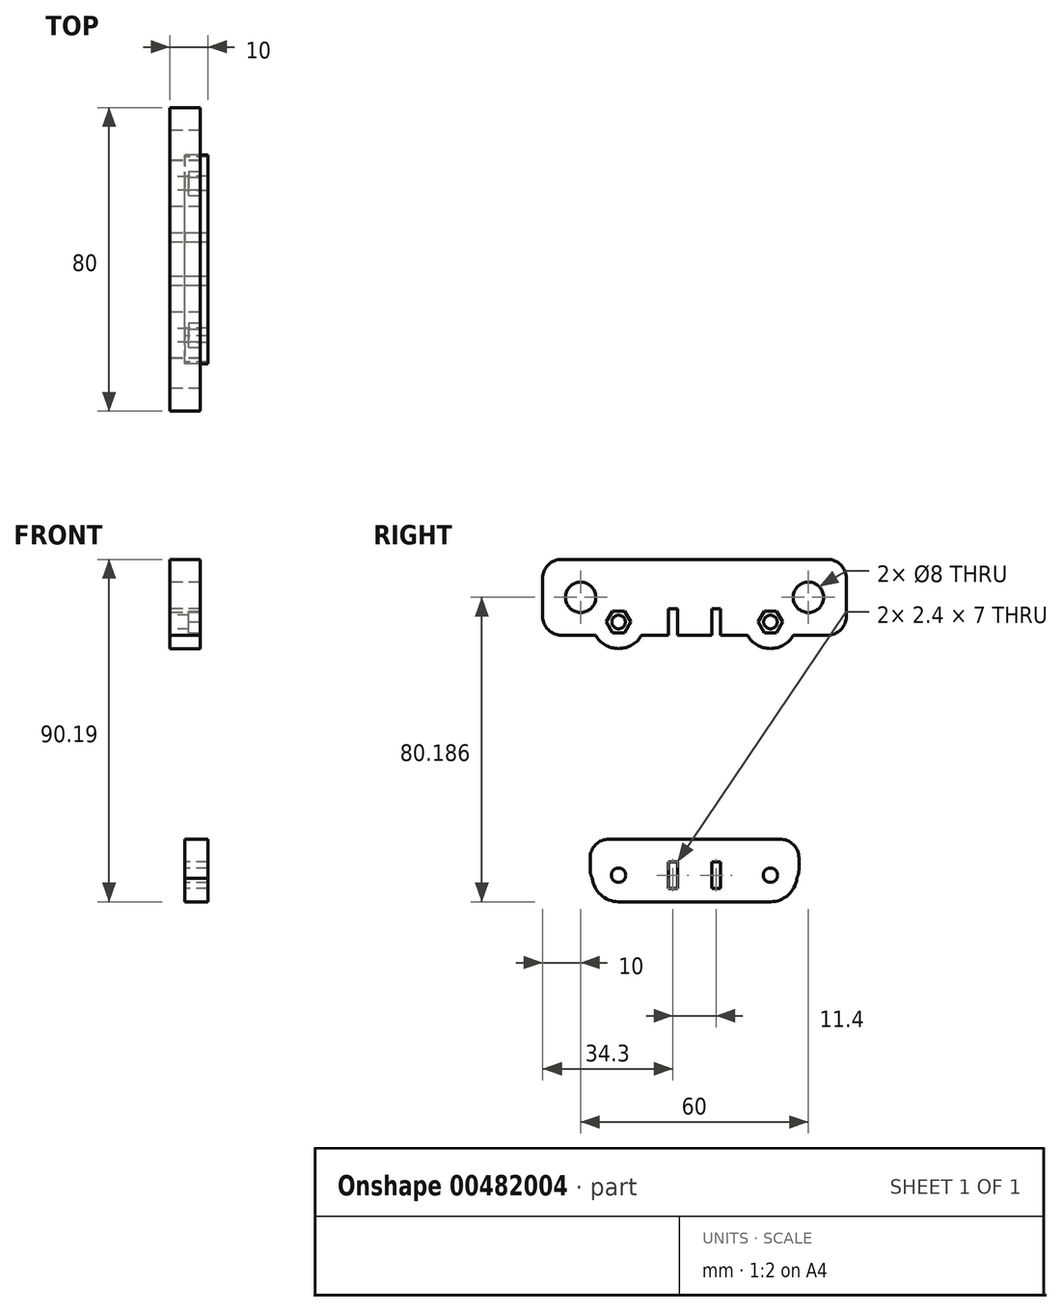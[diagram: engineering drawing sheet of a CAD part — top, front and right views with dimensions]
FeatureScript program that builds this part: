
annotation { "Feature Type Name" : "Feature", "Feature Type Description" : "" }
export const myFeature = defineFeature(function(context is Context, id is Id, definition is map)
    precondition{}
    {
        {
            var Q0;
            Q0=qCreatedBy(makeId("Right.planeOp"),FACE);
            var sketch = newSketch(context, id + "F0", { "sketchPlane" : qUnion([Q0])});
            skLineSegment(sketch, "E0", {"start": v(0, 142.5) * mm, "end": v(0, -139.74) * mm, "construction": true});
            skLineSegment(sketch, "E1.bottom", {"start": v(-35, 25) * mm, "end": v(35, 25) * mm});
            skLineSegment(sketch, "E1.top", {"start": v(-40, -25) * mm, "end": v(40, -25) * mm});
            skLineSegment(sketch, "E1.left", {"start": v(-40, 20) * mm, "end": v(-40, -25) * mm});
            skLineSegment(sketch, "E1.right", {"start": v(40, 20) * mm, "end": v(40, -25) * mm});
            skPoint(sketch, "E1.middle", {"position": v(0, 0) * mm});
            skCircle(sketch, "E2", {"center": v(-30, 13) * mm, "radius": 4 * mm});
            skCircle(sketch, "E3", {"center": v(30, 13) * mm, "radius": 4 * mm});
            skCircle(sketch, "E4", {"center": v(-30, -13) * mm, "radius": 5 * mm});
            skCircle(sketch, "E5", {"center": v(30, -13) * mm, "radius": 5 * mm});
            skPoint(sketch, "E6.visualSharp", {"position": v(-40, 25) * mm});
            skArc(sketch, "E6.filletArc", {"start": v(-35, 25) * mm, "mid": v(-38.54, 23.54) * mm, "end": v(-40, 20) * mm});
            skPoint(sketch, "E7.visualSharp", {"position": v(40, 25) * mm});
            skArc(sketch, "E7.filletArc", {"start": v(40, 20) * mm, "mid": v(38.54, 23.54) * mm, "end": v(35, 25) * mm});
            skLineSegment(sketch, "E8.bottom", {"start": v(-11, 25) * mm, "end": v(11, 25) * mm});
            skLineSegment(sketch, "E8.top", {"start": v(-9, 8) * mm, "end": v(9, 8) * mm});
            skLineSegment(sketch, "E8.left", {"start": v(-11, 25) * mm, "end": v(-11, 10) * mm});
            skLineSegment(sketch, "E8.right", {"start": v(11, 25) * mm, "end": v(11, 10) * mm});
            skPoint(sketch, "E8.middle", {"position": v(0, 16.5) * mm});
            skPoint(sketch, "E9.visualSharp", {"position": v(11, 8) * mm});
            skArc(sketch, "E9.filletArc", {"start": v(9, 8) * mm, "mid": v(10.41, 8.59) * mm, "end": v(11, 10) * mm});
            skPoint(sketch, "E10.visualSharp", {"position": v(-11, 8) * mm});
            skArc(sketch, "E10.filletArc", {"start": v(-11, 10) * mm, "mid": v(-10.41, 8.59) * mm, "end": v(-9, 8) * mm});
            skSolve(sketch);
        }
        {
            var Q0;
            Q0=makeQuery(id+"F0.imprint","IMPRINT",FACE,{"disambiguationData":[TD([[makeQuery(id+"F0.imprint","IMPRINT",EDGE,{"derivedFrom":sQuery(id+"F0.wireOp",EDGE,"E1.bottom")}),-1.0]])]});
            extrude(context, id + "F1", {"entities" : qUnion([Q0]), "endBound" : BoundingType.SYMMETRIC, "depth" : 8 * mm});
        }
        {
            var Q0;
            {var subQ0=sQuery(id+"F0.wireOp",EDGE,"E1.bottom");Q0=makeQuery(id+"F1.opExtrude","SWEPT_FACE",FACE,{"disambiguationData":[OSD([subQ0]),TDD([makeQuery(id+"F0.imprint","IMPRINT",EDGE,{"disambiguationData":[TD([[makeQuery(id+"F0.imprint","INTERSECT",VERTEX,{"derivedFrom":[subQ0,sQuery(id+"F0.wireOp",EDGE,"E7.filletArc")]}),1.0]])],"derivedFrom":subQ0})])]});}
            var sketch = newSketch(context, id + "F2", { "sketchPlane" : qUnion([Q0])});
            skCircle(sketch, "E11", {"center": v(0, 30) * mm, "radius": 1.4 * mm});
            skCircle(sketch, "E12", {"center": v(0, 24) * mm, "radius": 1.4 * mm});
            skCircle(sketch, "E13", {"center": v(0, -24) * mm, "radius": 1.4 * mm});
            skCircle(sketch, "E14", {"center": v(0, -30) * mm, "radius": 1.4 * mm});
            skLineSegment(sketch, "E15", {"start": v(-76.86, 0) * mm, "end": v(82.98, 0) * mm, "construction": true});
            skSolve(sketch);
        }
        {
            var Q0;
            Q0=qSketchRegion(id+"F2",true);
            extrude(context, id + "F3", {"entities" : qUnion([Q0]), "operationType" : NewBodyOperationType.REMOVE, "oppositeDirection" : true, "depth" : 13 * mm});
        }
        {
            var Q0;
            Q0=qCreatedBy(makeId("Right.planeOp"),FACE);
            var sketch = newSketch(context, id + "F4", { "sketchPlane" : qUnion([Q0])});
            skLineSegment(sketch, "E16", {"start": v(0, 90) * mm, "end": v(0, 27.03) * mm, "construction": true});
            skCircle(sketch, "E17", {"center": v(-30, 70.19) * mm, "radius": 4 * mm});
            skCircle(sketch, "E18", {"center": v(30, 70.19) * mm, "radius": 4 * mm});
            skLineSegment(sketch, "E19.bottom", {"start": v(-35, 80.19) * mm, "end": v(35, 80.19) * mm});
            skLineSegment(sketch, "E19.top", {"start": v(-35, 60.19) * mm, "end": v(-26.06, 60.19) * mm});
            skLineSegment(sketch, "E19.left", {"start": v(-40, 75.19) * mm, "end": v(-40, 65.19) * mm});
            skLineSegment(sketch, "E19.right", {"start": v(40, 75.19) * mm, "end": v(40, 65.19) * mm});
            skPoint(sketch, "E19.middle", {"position": v(0, 70.19) * mm});
            skPoint(sketch, "E20.visualSharp", {"position": v(-40, 80.19) * mm});
            skArc(sketch, "E20.filletArc", {"start": v(-35, 80.19) * mm, "mid": v(-38.54, 78.72) * mm, "end": v(-40, 75.19) * mm});
            skPoint(sketch, "E21.visualSharp", {"position": v(-40, 60.19) * mm});
            skArc(sketch, "E21.filletArc", {"start": v(-40, 65.19) * mm, "mid": v(-38.54, 61.65) * mm, "end": v(-35, 60.19) * mm});
            skPoint(sketch, "E22.visualSharp", {"position": v(40, 80.19) * mm});
            skArc(sketch, "E22.filletArc", {"start": v(40, 75.19) * mm, "mid": v(38.54, 78.72) * mm, "end": v(35, 80.19) * mm});
            skPoint(sketch, "E23.visualSharp", {"position": v(40, 60.19) * mm});
            skArc(sketch, "E23.filletArc", {"start": v(35, 60.19) * mm, "mid": v(38.54, 61.65) * mm, "end": v(40, 65.19) * mm});
            skLineSegment(sketch, "E24.bottom", {"start": v(-11, 80.19) * mm, "end": v(11, 80.19) * mm});
            skPoint(sketch, "E24.middle", {"position": v(0, 76.69) * mm});
            skLineSegment(sketch, "E25", {"start": v(-87.97, 70.19) * mm, "end": v(-87.97, 70.19) * mm});
            skPoint(sketch, "E25.endSnap0", {"position": v(40, 70.19) * mm});
            skLineSegment(sketch, "E26.bottom", {"start": v(-6.9, 67.19) * mm, "end": v(-4.5, 67.19) * mm});
            skLineSegment(sketch, "E26.top", {"start": v(-6.9, 60.19) * mm, "end": v(-4.5, 60.19) * mm});
            skLineSegment(sketch, "E26.left", {"start": v(-6.9, 67.19) * mm, "end": v(-6.9, 60.19) * mm});
            skLineSegment(sketch, "E26.right", {"start": v(-4.5, 67.19) * mm, "end": v(-4.5, 60.19) * mm});
            skLineSegment(sketch, "E27.bottom", {"start": v(4.5, 67.19) * mm, "end": v(6.9, 67.19) * mm});
            skLineSegment(sketch, "E27.top", {"start": v(4.5, 60.19) * mm, "end": v(6.9, 60.19) * mm});
            skLineSegment(sketch, "E27.left", {"start": v(4.5, 67.19) * mm, "end": v(4.5, 60.19) * mm});
            skLineSegment(sketch, "E27.right", {"start": v(6.9, 67.19) * mm, "end": v(6.9, 60.19) * mm});
            skCircle(sketch, "E28", {"center": v(-20, 63.69) * mm, "radius": 1.8 * mm});
            skCircle(sketch, "E29", {"center": v(20, 63.69) * mm, "radius": 1.8 * mm});
            skArc(sketch, "E30", {"start": v(-26.06, 60.19) * mm, "mid": v(-20, 56.69) * mm, "end": v(-13.94, 60.19) * mm});
            skArc(sketch, "E31.MirrorC", {"start": v(26.06, 60.19) * mm, "mid": v(20, 56.69) * mm, "end": v(13.94, 60.19) * mm});
            skLineSegment(sketch, "E32.trimOffspring", {"start": v(-13.94, 60.19) * mm, "end": v(13.94, 60.19) * mm});
            skLineSegment(sketch, "E33.trimOffspring", {"start": v(26.06, 60.19) * mm, "end": v(35, 60.19) * mm});
            skSolve(sketch);
        }
        {
            var Q0;
            Q0=makeQuery(id+"F4.imprint","IMPRINT",FACE,{"disambiguationData":[TD([[makeQuery(id+"F4.imprint","IMPRINT",EDGE,{"derivedFrom":sQuery(id+"F4.wireOp",EDGE,"E17")}),-1.0]])]});
            extrude(context, id + "F5", {"entities" : qUnion([Q0]), "endBound" : BoundingType.SYMMETRIC, "depth" : 8 * mm});
        }
        {
            var Q0;
            Q0=makeQuery(id+"F5.opExtrude","CAP_FACE",FACE,{"disambiguationData":[OSD([sQuery(id+"F4.wireOp",EDGE,"E17"),sQuery(id+"F4.wireOp",EDGE,"E18"),sQuery(id+"F4.wireOp",EDGE,"E19.bottom"),sQuery(id+"F4.wireOp",EDGE,"E19.top"),sQuery(id+"F4.wireOp",EDGE,"E19.left"),sQuery(id+"F4.wireOp",EDGE,"E19.right"),sQuery(id+"F4.wireOp",EDGE,"E20.filletArc"),sQuery(id+"F4.wireOp",EDGE,"E21.filletArc"),sQuery(id+"F4.wireOp",EDGE,"E22.filletArc"),sQuery(id+"F4.wireOp",EDGE,"E23.filletArc"),sQuery(id+"F4.wireOp",EDGE,"E24.bottom"),sQuery(id+"F4.wireOp",EDGE,"E26.bottom"),sQuery(id+"F4.wireOp",EDGE,"E26.left"),sQuery(id+"F4.wireOp",EDGE,"E26.right"),sQuery(id+"F4.wireOp",EDGE,"E27.bottom"),sQuery(id+"F4.wireOp",EDGE,"E27.left"),sQuery(id+"F4.wireOp",EDGE,"E27.right"),sQuery(id+"F4.wireOp",EDGE,"E28"),sQuery(id+"F4.wireOp",EDGE,"E29")])],"isStart":false});
            var sketch = newSketch(context, id + "F6", { "sketchPlane" : qUnion([Q0])});
            skCircle(sketch, "E34.cCircle", {"center": v(20, 63.69) * mm, "radius": 2.8 * mm, "construction": true});
            skLineSegment(sketch, "E34.0", {"start": v(18.38, 66.49) * mm, "end": v(21.62, 66.49) * mm});
            skLineSegment(sketch, "E34.1", {"start": v(21.62, 66.49) * mm, "end": v(23.23, 63.69) * mm});
            skLineSegment(sketch, "E34.2", {"start": v(23.23, 63.69) * mm, "end": v(21.62, 60.89) * mm});
            skLineSegment(sketch, "E34.3", {"start": v(21.62, 60.89) * mm, "end": v(18.38, 60.89) * mm});
            skLineSegment(sketch, "E34.4", {"start": v(18.38, 60.89) * mm, "end": v(16.77, 63.69) * mm});
            skLineSegment(sketch, "E34.5", {"start": v(16.77, 63.69) * mm, "end": v(18.38, 66.49) * mm});
            skPoint(sketch, "E34.0.midPoint", {"position": v(20, 66.49) * mm});
            skCircle(sketch, "E35.cCircle", {"center": v(-20, 63.69) * mm, "radius": 2.8 * mm, "construction": true});
            skLineSegment(sketch, "E35.0", {"start": v(-21.62, 66.49) * mm, "end": v(-18.38, 66.49) * mm});
            skLineSegment(sketch, "E35.1", {"start": v(-18.38, 66.49) * mm, "end": v(-16.77, 63.69) * mm});
            skLineSegment(sketch, "E35.2", {"start": v(-16.77, 63.69) * mm, "end": v(-18.38, 60.89) * mm});
            skLineSegment(sketch, "E35.3", {"start": v(-18.38, 60.89) * mm, "end": v(-21.62, 60.89) * mm});
            skLineSegment(sketch, "E35.4", {"start": v(-21.62, 60.89) * mm, "end": v(-23.23, 63.69) * mm});
            skLineSegment(sketch, "E35.5", {"start": v(-23.23, 63.69) * mm, "end": v(-21.62, 66.49) * mm});
            skPoint(sketch, "E35.0.midPoint", {"position": v(-20, 66.49) * mm});
            skSolve(sketch);
        }
        {
            var Q0;
            Q0=qSketchRegion(id+"F6",true);
            extrude(context, id + "F7", {"entities" : qUnion([Q0]), "operationType" : NewBodyOperationType.REMOVE, "oppositeDirection" : true, "depth" : 3 * mm});
        }
        {
            var Q0;
            Q0=qCreatedBy(makeId("Right.planeOp"),FACE);
            var sketch = newSketch(context, id + "F8", { "sketchPlane" : qUnion([Q0])});
            skLineSegment(sketch, "E36.bottom", {"start": v(-22.5, 6.5) * mm, "end": v(22.5, 6.5) * mm});
            skLineSegment(sketch, "E36.top", {"start": v(-6.9, -6.5) * mm, "end": v(-4.5, -6.5) * mm});
            skLineSegment(sketch, "E36.left", {"start": v(-27.5, 1.5) * mm, "end": v(-27.5, -1.5) * mm});
            skLineSegment(sketch, "E36.right", {"start": v(27.5, 1.5) * mm, "end": v(27.5, -1.5) * mm});
            skPoint(sketch, "E36.middle", {"position": v(0, 0) * mm});
            skPoint(sketch, "E37.visualSharp", {"position": v(-27.5, 6.5) * mm});
            skArc(sketch, "E37.filletArc", {"start": v(-22.5, 6.5) * mm, "mid": v(-26.04, 5.04) * mm, "end": v(-27.5, 1.5) * mm});
            skPoint(sketch, "E38.visualSharp", {"position": v(-27.5, -6.5) * mm});
            skArc(sketch, "E38.filletArc", {"start": v(-27.5, -1.5) * mm, "mid": v(-27.36, -2.66) * mm, "end": v(-26.96, -3.76) * mm});
            skPoint(sketch, "E39.visualSharp", {"position": v(27.5, 6.5) * mm});
            skArc(sketch, "E39.filletArc", {"start": v(27.5, 1.5) * mm, "mid": v(26.04, 5.04) * mm, "end": v(22.5, 6.5) * mm});
            skPoint(sketch, "E40.visualSharp", {"position": v(27.5, -6.5) * mm});
            skArc(sketch, "E40.filletArc", {"start": v(26.96, -3.76) * mm, "mid": v(27.36, -2.66) * mm, "end": v(27.5, -1.5) * mm});
            skLineSegment(sketch, "E41.bottom", {"start": v(-6.9, 0.5) * mm, "end": v(-4.5, 0.5) * mm});
            skLineSegment(sketch, "E41.left", {"start": v(-6.9, 0.5) * mm, "end": v(-6.9, -6.5) * mm});
            skLineSegment(sketch, "E41.right", {"start": v(-4.5, 0.5) * mm, "end": v(-4.5, -6.5) * mm});
            skLineSegment(sketch, "E42.MirrorCS", {"start": v(6.9, 0.5) * mm, "end": v(4.5, 0.5) * mm});
            skLineSegment(sketch, "E43.MirrorCS", {"start": v(6.9, -6.5) * mm, "end": v(4.5, -6.5) * mm});
            skLineSegment(sketch, "E44.MirrorCS", {"start": v(4.5, 0.5) * mm, "end": v(4.5, -6.5) * mm});
            skLineSegment(sketch, "E45.MirrorCS", {"start": v(6.9, 0.5) * mm, "end": v(6.9, -6.5) * mm});
            skCircle(sketch, "E46", {"center": v(20, -3) * mm, "radius": 1.9 * mm});
            skCircle(sketch, "E47.MirrorC", {"center": v(-20, -3) * mm, "radius": 1.9 * mm});
            skArc(sketch, "E48", {"start": v(-26.96, -3.76) * mm, "mid": v(-24.64, -8.24) * mm, "end": v(-19.91, -10) * mm});
            skArc(sketch, "E49.MirrorC", {"start": v(26.96, -3.76) * mm, "mid": v(24.67, -8.21) * mm, "end": v(20, -10) * mm});
            skPoint(sketch, "E50.orphan", {"position": v(22.5, -6.5) * mm});
            skLineSegment(sketch, "E51", {"start": v(-20.09, -10) * mm, "end": v(20, -10) * mm});
            skLineSegment(sketch, "E52.trimOffspring", {"start": v(4.5, -6.5) * mm, "end": v(6.9, -6.5) * mm});
            skSolve(sketch);
        }
        {
            var Q0;
            Q0=makeQuery(id+"F8.imprint","IMPRINT",FACE,{"disambiguationData":[TD([[makeQuery(id+"F8.imprint","IMPRINT",EDGE,{"derivedFrom":sQuery(id+"F8.wireOp",EDGE,"E36.bottom")}),-1.0]])]});
            extrude(context, id + "F9", {"entities" : qUnion([Q0]), "depth" : 6 * mm});
        }
        {
            var Q0;
            Q0=makeQuery(id+"F1.opExtrude","SWEPT_BODY",BODY,{"disambiguationData":[OSD([sQuery(id+"F0.wireOp",EDGE,"E1.bottom"),sQuery(id+"F0.wireOp",EDGE,"E1.top"),sQuery(id+"F0.wireOp",EDGE,"E1.left"),sQuery(id+"F0.wireOp",EDGE,"E1.right"),sQuery(id+"F0.wireOp",EDGE,"E2"),sQuery(id+"F0.wireOp",EDGE,"E3"),sQuery(id+"F0.wireOp",EDGE,"E4"),sQuery(id+"F0.wireOp",EDGE,"E5"),sQuery(id+"F0.wireOp",EDGE,"E6.filletArc"),sQuery(id+"F0.wireOp",EDGE,"E7.filletArc"),sQuery(id+"F0.wireOp",EDGE,"E8.top"),sQuery(id+"F0.wireOp",EDGE,"E8.left"),sQuery(id+"F0.wireOp",EDGE,"E8.right"),sQuery(id+"F0.wireOp",EDGE,"E9.filletArc"),sQuery(id+"F0.wireOp",EDGE,"E10.filletArc")])]});
            deleteBodies(context, id + "F10", {"entities" : qUnion([Q0])});
        }
    });
